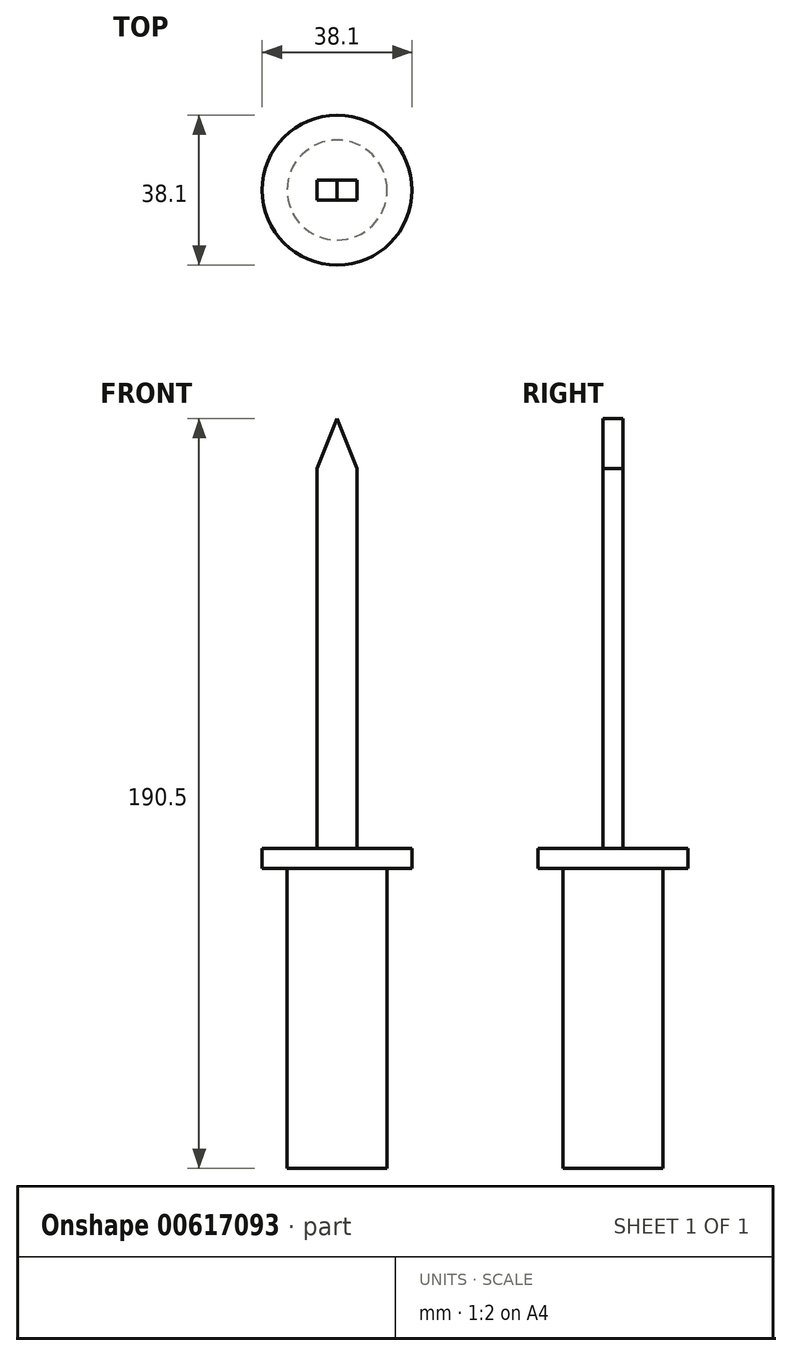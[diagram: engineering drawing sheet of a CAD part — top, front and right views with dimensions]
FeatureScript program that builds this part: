
annotation { "Feature Type Name" : "Feature", "Feature Type Description" : "" }
export const myFeature = defineFeature(function(context is Context, id is Id, definition is map)
    precondition{}
    {
        {
            var Q0;
            Q0=qCreatedBy(makeId("Top.planeOp"),FACE);
            var sketch = newSketch(context, id + "F0", { "sketchPlane" : qUnion([Q0])});
            skCircle(sketch, "E0", {"center": v(0, 0) * mm, "radius": 12.7 * mm});
            skSolve(sketch);
        }
        {
            var Q0;
            Q0 = qSketchRegion(id + "F0", true);
            extrude(context, id + "F1", {"entities" : qUnion([Q0]), "oppositeDirection" : true, "depth" : 76.2 * mm, "offsetDistance" : 25.4 * mm});
        }
        {
            var Q0;
            Q0=qCreatedBy(makeId("Top.planeOp"),FACE);
            var sketch = newSketch(context, id + "F2", { "sketchPlane" : qUnion([Q0])});
            skCircle(sketch, "E1", {"center": v(0, 0) * mm, "radius": 19.05 * mm});
            skSolve(sketch);
        }
        {
            var Q0;
            Q0 = qSketchRegion(id + "F2", true);
            extrude(context, id + "F3", {"entities" : qUnion([Q0]), "operationType" : NewBodyOperationType.ADD, "depth" : 5.08 * mm, "offsetDistance" : 25.4 * mm});
        }
        {
            var Q0;
            Q0=qCreatedBy(makeId("Front.planeOp"),FACE);
            var sketch = newSketch(context, id + "F4", { "sketchPlane" : qUnion([Q0])});
            skLineSegment(sketch, "E2", {"start": v(0, 0) * mm, "end": v(0, 114.3) * mm});
            skLineSegment(sketch, "E3", {"start": v(0, 0) * mm, "end": v(5.08, 0) * mm});
            skLineSegment(sketch, "E4", {"start": v(0, 0) * mm, "end": v(-5.08, 0) * mm});
            skLineSegment(sketch, "E5", {"start": v(-5.08, 0) * mm, "end": v(-5.08, 101.6) * mm});
            skLineSegment(sketch, "E6", {"start": v(-5.08, 101.6) * mm, "end": v(0, 114.3) * mm});
            skLineSegment(sketch, "E7", {"start": v(5.08, 0) * mm, "end": v(5.08, 101.6) * mm});
            skLineSegment(sketch, "E8", {"start": v(5.08, 101.6) * mm, "end": v(0, 114.3) * mm});
            skSolve(sketch);
        }
        {
            var Q0;
            Q0 = qSketchRegion(id + "F4", true);
            extrude(context, id + "F5", {"entities" : qUnion([Q0]), "operationType" : NewBodyOperationType.ADD, "oppositeDirection" : true, "depth" : 2.54 * mm, "offsetDistance" : 25.4 * mm});
        }
        {
            var Q0;
            Q0=qCreatedBy(makeId("Front.planeOp"),FACE);
            var sketch = newSketch(context, id + "F6", { "sketchPlane" : qUnion([Q0])});
            skLineSegment(sketch, "E9", {"start": v(0, 0) * mm, "end": v(0, 114.3) * mm});
            skLineSegment(sketch, "E10", {"start": v(0, 0) * mm, "end": v(5.08, 0) * mm});
            skLineSegment(sketch, "E11", {"start": v(5.08, 0) * mm, "end": v(5.08, 101.6) * mm});
            skLineSegment(sketch, "E12", {"start": v(5.08, 101.6) * mm, "end": v(0, 114.3) * mm});
            skLineSegment(sketch, "E13", {"start": v(0, 0) * mm, "end": v(-5.08, 0) * mm});
            skLineSegment(sketch, "E14", {"start": v(-5.08, 0) * mm, "end": v(-5.08, 101.6) * mm});
            skLineSegment(sketch, "E15", {"start": v(-5.08, 101.6) * mm, "end": v(0, 114.3) * mm});
            skSolve(sketch);
        }
        {
            var Q0;
            Q0 = qSketchRegion(id + "F6", true);
            extrude(context, id + "F7", {"entities" : qUnion([Q0]), "operationType" : NewBodyOperationType.ADD, "depth" : 2.54 * mm, "offsetDistance" : 25.4 * mm});
        }
    });
